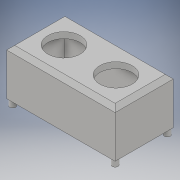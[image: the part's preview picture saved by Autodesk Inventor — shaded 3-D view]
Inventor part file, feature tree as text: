
AUTODESK INVENTOR PART (.ipt)
format: ipt  version: 2019 (Build 230136000, 136)  size: 364,032 bytes
history: native  units: mm
features: sketch x10, extrude x9, projected_geometry x9, chamfer x4
ambient origin geometry x8: Origin, YZ Plane, XZ Plane, XY Plane, X Axis, Y Axis, Z Axis, Center Point
bodies: Solid1 (feature_tree)
feature tree (32):
  extrude  "Extrusion1"  Depth=16.1mm
  extrude  "Extrusion11"  Depth=29.0mm
  extrude  "Extrusion12"  Depth=54.0mm
  chamfer  "Chamfer5"  Distance=3.0mm
  extrude  "Extrusion2"  Depth=48.0mm
  extrude  "Extrusion3"  Depth=51.0mm
  extrude  "Extrusion4"  Depth=3.0mm
  extrude  "Extrusion5"  Depth=3.0mm TaperAngle=0.0deg
  chamfer  "Chamfer1"  Distance=3.5mm
  chamfer  "Chamfer2"  Distance=4.0mm
  extrude  "Extrusion6"  Depth=3.0mm
  extrude  "Extrusion7"  Depth=3.0mm
  chamfer  "Chamfer3"  Distance=20.0mm
  sketch  "Sketch8"  dims[d13=25.0mm d14=0.0mm d15=51.0mm]
  sketch  "Sketch1"  dims[d0=16.1mm d1=16.1mm]
  sketch  "Sketch2"  dims[d2=25.9mm d3=29.0mm]
  sketch  "Sketch3"  dims[d4=54.0mm d5=14.5mm]
  sketch  "Sketch4"  dims[d6=14.5mm]
  sketch  "Sketch5"  dims[d7=14.05mm]
  projected_geometry  "Projected Loop1"
  projected_geometry  "Projected Loop2"
  projected_geometry  "Projected Loop3"
  projected_geometry  "Projected Loop4"
  sketch  "Sketch6"  dims[d8=14.05mm d9=3.0mm d10=0.0mm]
  projected_geometry  "Projected Loop5"
  projected_geometry  "Projected Loop6"
  sketch  "Sketch7"  dims[d11=23.0mm d12=48.0mm]
  projected_geometry  "Projected Loop7"
  projected_geometry  "Projected Loop8"
  sketch  "Sketch12"  dims[d16=3.0mm d17=0.0mm d18=45.0mm]
  projected_geometry  "Projected Loop12"
  sketch  "Sketch13"  dims[d19=48.0mm d20=15.0mm d21=0.0mm d22=3.5mm d23=4.0mm d24=4.0mm d25=4.0mm d26=20.0mm d28=40.0mm d29=20.0mm d31=37.0mm d34=10.0mm d35=0.0mm d36=2.0mm d37=2.0mm d38=45.0deg d39=2.0mm d40=2.0mm d41=45.0deg d42=6.0mm d43=20.0mm d45=40.0mm d46=20.0mm d48=37.0mm d51=10.0mm d52=0.0mm d53=4.0mm d54=15.0mm d55=3.0mm d56=18.0mm d57=18.0mm d58=16.0mm d59=0.0mm d60=2.0mm d61=2.0mm d62=45.0deg d63=6.0mm d85=3.0mm d86=3.0mm d87=3.0mm d88=3.0mm d89=20.0mm d90=0.0mm d91=1.5mm d92=1.5mm d93=2.9mm d94=20.0mm d96=51.0mm d97=20.0mm d99=26.0mm d102=3.0mm d103=0.0mm d104=2.0mm d105=2.0mm d106=45.0deg]
